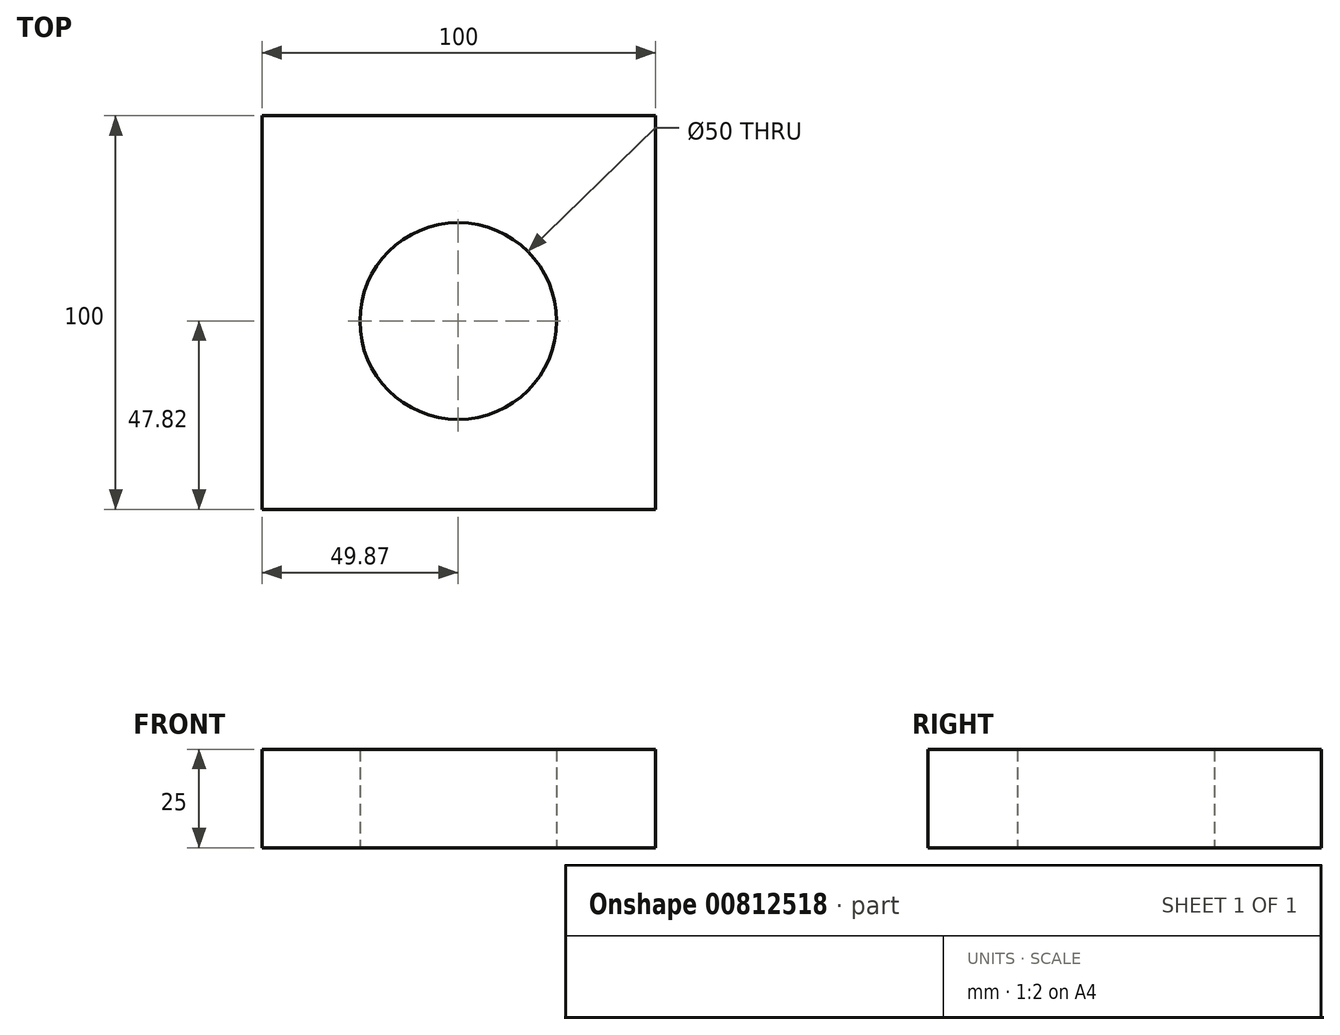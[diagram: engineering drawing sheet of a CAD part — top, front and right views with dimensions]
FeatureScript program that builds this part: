
annotation { "Feature Type Name" : "Feature", "Feature Type Description" : "" }
export const myFeature = defineFeature(function(context is Context, id is Id, definition is map)
    precondition{}
    {
        {
            var Q0;
            Q0=qCreatedBy(makeId("Top.planeOp"),FACE);
            var sketch = newSketch(context, id + "F0", { "sketchPlane" : qUnion([Q0])});
            skLineSegment(sketch, "E0.bottom", {"start": v(-49.87, 52.18) * mm, "end": v(50.13, 52.18) * mm});
            skLineSegment(sketch, "E0.top", {"start": v(-49.87, -47.82) * mm, "end": v(50.13, -47.82) * mm});
            skLineSegment(sketch, "E0.left", {"start": v(-49.87, 52.18) * mm, "end": v(-49.87, -47.82) * mm});
            skLineSegment(sketch, "E0.right", {"start": v(50.13, 52.18) * mm, "end": v(50.13, -47.82) * mm});
            skCircle(sketch, "E1", {"center": v(0, 0) * mm, "radius": 25 * mm});
            skSolve(sketch);
        }
        {
            var Q0;
            Q0=makeQuery(id+"F0.imprint","IMPRINT",FACE,{"disambiguationData":[TD([[makeQuery(id+"F0.imprint","IMPRINT",EDGE,{"derivedFrom":sQuery(id+"F0.wireOp",EDGE,"E0.bottom")}),-1.0]])]});
            extrude(context, id + "F1", {"entities" : qUnion([Q0]), "depth" : 25 * mm, "offsetDistance" : 25 * mm});
        }
        {
            var Q0;
            Q0=sQuery(id+"F0.wireOp",EDGE,"E1");
            extrude(context, id + "F2", {"bodyType" : ToolBodyType.SURFACE, "surfaceEntities" : qUnion([Q0]), "depth" : 25 * mm, "offsetDistance" : 25 * mm});
        }
    });
